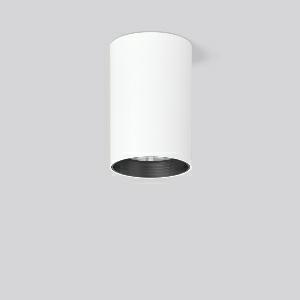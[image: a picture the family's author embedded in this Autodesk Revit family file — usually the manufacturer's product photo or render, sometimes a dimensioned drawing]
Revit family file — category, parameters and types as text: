
# Revit family: heledon_maxi_a_931228_002_2_76_6aa0
name_source: partatom
category: Lighting Fixtures
units: mm (PartAtom-declared; Revit-internal decimal feet)

## family parameters
Cut with Voids When Loaded = No
Host = Face
Light Source = No
Part Type = Normal
Room Calculation Point = No
Round Connector Dimension = Use Diameter
Shared = No

## types (1)
- HELEDON maxi A (1 x LED Modul 927, 3350 lm, 2700)
    Apparent Load = 35 VA
    Approval mark = CE
    CIE Flux Codes = 96 100 100 100 100
    Color Rendering = 92
    Color Temperature = 2700
    Default Elevation = 1800 mm
    Description = Series: HELEDON maxi
Cylindrical surface-mounted downlight. Housing: die-cast aluminium, powder-coated. Internal ceiling frame polycarbonate with bayonet mounting. Black plastic ring and recessed LED to prevent glare from the side. Optical assembly with lens made of plastic (polycarbonate) for the best homogeneous light distribution - can be changed without tools. Best colour rendering index Ra>90. Suitable for Ceiling mounting. Easy installation with a separate ceiling frame with bayonet mounting and plug connection. Driver integrated. Connected via plug-in connector. High quality converter without flickering and stroboscopic effect. The following accessories can be mounted without use of tools: interchangeable lenses, decorative glasses, honeycomb louvre, clear and frosted diffusers, white interchangeable plastic ring. 
Colour: traffic white, matt (RAL 9016)
Diameter: 123 mm
Height: 183 mm
Lamp: LED
Socket: without socket
Colour temperature: 2700K
Colour rendering index (CRI): 92
System power: 35 W
Rated luminous flux: 3350 lm
Luminous efficiency: 96 lm/W
Control gear: Converter, dimmable, DALI
Protection class: I
Type of protection: IP 20
    Height = 183 mm
    Lamp = 1 x LED Modul 927
    Lamp Light Flux = 3350 lm
    Lamp count = 1
    Length = 123 mm
    Lifetime = 50000 h
    Luminous efficacy = 96 lm/W
    Manufacturer = RZB
    ModVariant = No
    Model = 931228.002.2.76
    Mounting Place = Ceiling
    Mounting Type = Surface mounted
    Number of Poles = 1
    OnlyDefault = Yes
    Power Factor = 1
    Product Name = HELEDON maxi A
    Product group = Surface mounted downlights
    ProductGroupID = 302
    Protection Class = Protection class I
    Protection Degree = IP 20
    RLX_Detail_Level = 1
    RLX_Emergency_Light_Flux = 0 lm
    RLX_Emergency_Type = 0
    RLX_Emergency_Type_DB = No
    RlxData = <blob elided: 96801 chars, md5=40cc8feb>
    Socket = socket
    Standby Power = 0 W
    System Light Flux = 3350 lm
    System Power = 35 W
    Type Comments = Product without accessories
    Type Image = 931193.002.jpg
    URL = http://relux.com
    VarID = ---
    Voltage = 230 V
    Voltage Range = 220-240 V
    Weight = 0.00 kg
    Width = 0 mm  [stored 0 ft]

note: [stored X ft] marks values corroborated as IEEE doubles in the binary element streams (Revit-internal decimal feet)

## geometry (parser evidence)
native form markers: Blend x4, Sweep x9
no freeform markers — native parametric forms only
